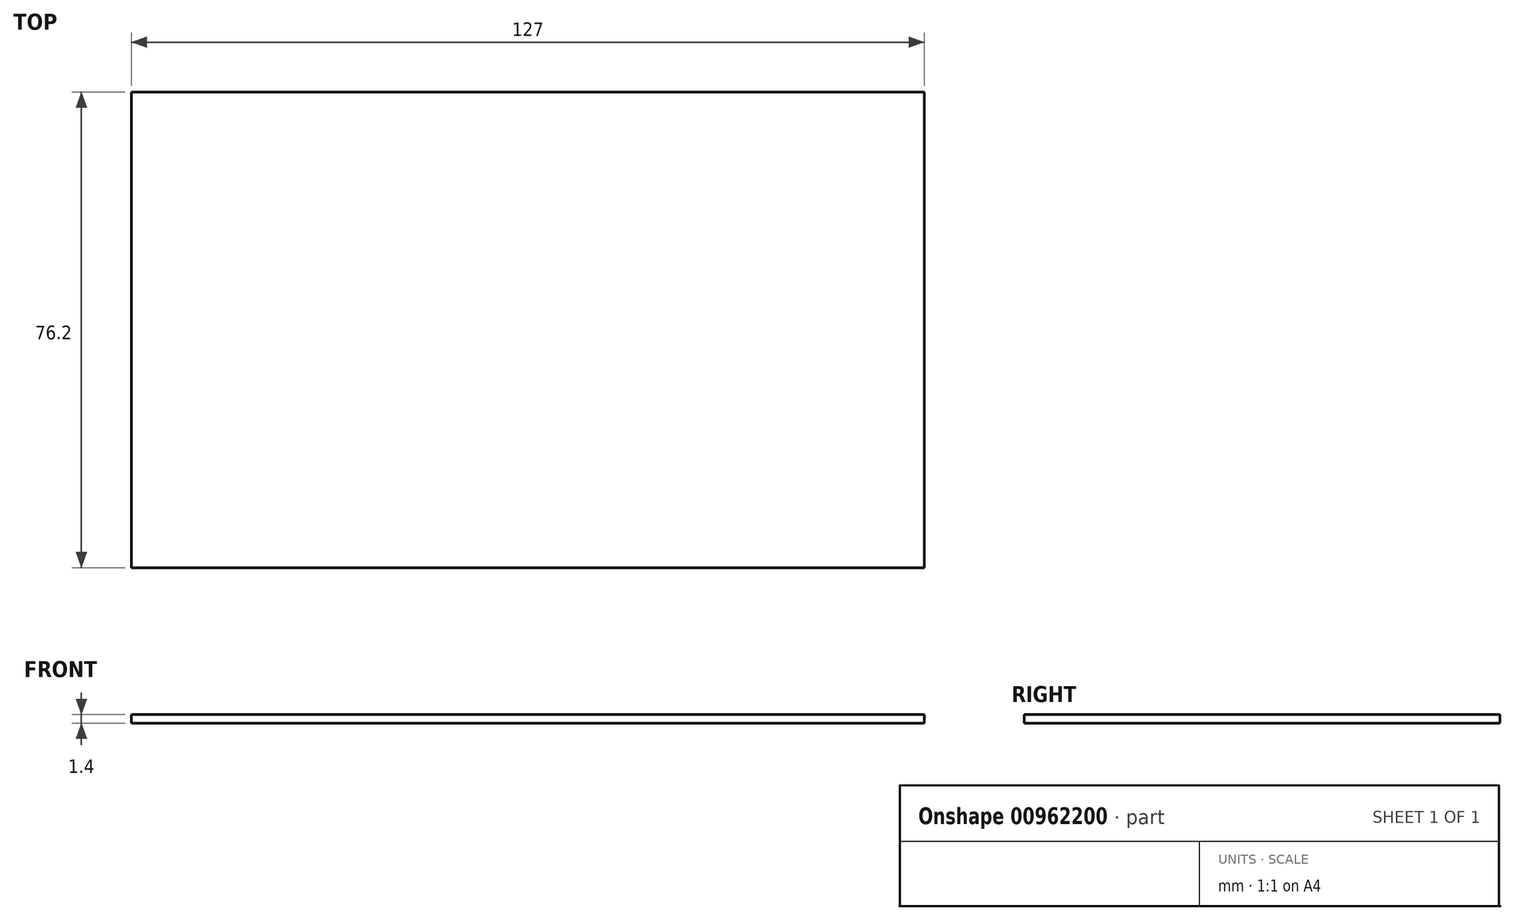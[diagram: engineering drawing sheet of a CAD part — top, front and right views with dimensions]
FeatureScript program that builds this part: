
annotation { "Feature Type Name" : "Feature", "Feature Type Description" : "" }
export const myFeature = defineFeature(function(context is Context, id is Id, definition is map)
    precondition{}
    {
        {
            var Q0;
            Q0=qCreatedBy(makeId("Top.planeOp"),FACE);
            var sketch = newSketch(context, id + "F0", { "sketchPlane" : qUnion([Q0])});
            skLineSegment(sketch, "E0.bottom", {"start": v(-127, 76.2) * mm, "end": v(0, 76.2) * mm});
            skLineSegment(sketch, "E0.top", {"start": v(-127, 0) * mm, "end": v(0, 0) * mm});
            skLineSegment(sketch, "E0.left", {"start": v(-127, 76.2) * mm, "end": v(-127, 0) * mm});
            skLineSegment(sketch, "E0.right", {"start": v(0, 76.2) * mm, "end": v(0, 0) * mm});
            skSolve(sketch);
        }
        {
            var Q0;
            Q0 = qSketchRegion(id + "F0", true);
            extrude(context, id + "F1", {"entities" : qUnion([Q0]), "depth" : 1.4 * mm, "offsetDistance" : 25.4 * mm});
        }
    });
